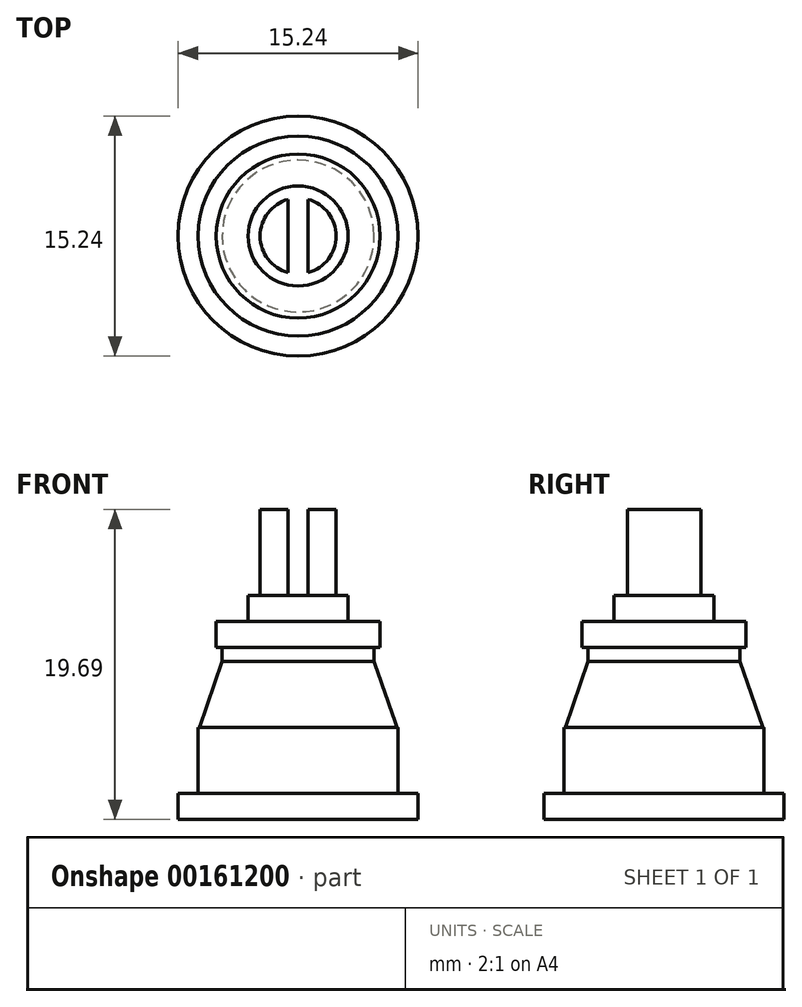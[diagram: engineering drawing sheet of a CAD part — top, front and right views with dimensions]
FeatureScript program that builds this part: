
annotation { "Feature Type Name" : "Feature", "Feature Type Description" : "" }
export const myFeature = defineFeature(function(context is Context, id is Id, definition is map)
    precondition{}
    {
        {
            var Q0;
            Q0=qCreatedBy(makeId("Front.planeOp"),FACE);
            var sketch = newSketch(context, id + "F0", { "sketchPlane" : qUnion([Q0])});
            skLineSegment(sketch, "E0", {"start": v(0, 29.57) * mm, "end": v(0, -1.96) * mm, "construction": true});
            skLineSegment(sketch, "E1", {"start": v(7.62, 0) * mm, "end": v(7.62, 1.65) * mm});
            skLineSegment(sketch, "E2", {"start": v(7.62, 1.65) * mm, "end": v(6.35, 1.65) * mm});
            skLineSegment(sketch, "E3", {"start": v(6.35, 1.65) * mm, "end": v(6.35, 5.84) * mm});
            skLineSegment(sketch, "E4", {"start": v(6.35, 5.84) * mm, "end": v(6.3, 5.84) * mm});
            skLineSegment(sketch, "E5", {"start": v(6.27, 5.86) * mm, "end": v(4.83, 10.03) * mm});
            skLineSegment(sketch, "E6", {"start": v(4.83, 10.03) * mm, "end": v(4.83, 10.03) * mm});
            skLineSegment(sketch, "E7", {"start": v(4.83, 10.03) * mm, "end": v(4.83, 10.92) * mm});
            skLineSegment(sketch, "E8", {"start": v(4.83, 10.92) * mm, "end": v(5.2, 10.92) * mm});
            skLineSegment(sketch, "E9", {"start": v(5.2, 10.92) * mm, "end": v(5.2, 12.57) * mm});
            skLineSegment(sketch, "E10", {"start": v(5.2, 12.57) * mm, "end": v(3.18, 12.57) * mm});
            skLineSegment(sketch, "E11", {"start": v(3.18, 12.57) * mm, "end": v(3.18, 14.22) * mm});
            skLineSegment(sketch, "E12", {"start": v(3.18, 14.22) * mm, "end": v(2.41, 14.22) * mm});
            skLineSegment(sketch, "E13", {"start": v(2.41, 14.22) * mm, "end": v(2.41, 19.69) * mm});
            skLineSegment(sketch, "E14", {"start": v(2.41, 19.69) * mm, "end": v(0, 19.69) * mm});
            skLineSegment(sketch, "E15", {"start": v(7.62, 0) * mm, "end": v(0, 0) * mm});
            skPoint(sketch, "E16.visualSharp", {"position": v(6.27, 5.84) * mm});
            skArc(sketch, "E16.filletArc", {"start": v(6.27, 5.86) * mm, "mid": v(6.28, 5.85) * mm, "end": v(6.3, 5.84) * mm});
            skLineSegment(sketch, "E17", {"start": v(0, 19.69) * mm, "end": v(0, 0) * mm});
            skLineSegment(sketch, "E18", {"start": v(0, 14.22) * mm, "end": v(0.64, 14.22) * mm});
            skLineSegment(sketch, "E19", {"start": v(0.64, 14.22) * mm, "end": v(0.64, 19.69) * mm});
            skLineSegment(sketch, "E20", {"start": v(0, 19.69) * mm, "end": v(-0.64, 19.69) * mm});
            skLineSegment(sketch, "E21", {"start": v(-0.64, 19.69) * mm, "end": v(-0.63, 14.22) * mm});
            skLineSegment(sketch, "E22", {"start": v(-0.63, 14.22) * mm, "end": v(0, 14.22) * mm});
            skSolve(sketch);
        }
        {
            var Q0;
            Q0=makeQuery(id+"F0.imprint","IMPRINT",FACE,{"disambiguationData":[TD([[makeQuery(id+"F0.imprint","IMPRINT",EDGE,{"derivedFrom":sQuery(id+"F0.wireOp",EDGE,"E1")}),1.0]])]});
            var Q1;
            Q1=sQuery(id+"F0.wireOp",EDGE,"E0");
            revolve(context, id + "F1", {"entities" : qUnion([Q0]), "axis" : qUnion([Q1]), "revolveType" : RevolveType.FULL});
        }
        {
            var Q0;
            {var subQ0=sQuery(id+"F0.wireOp",EDGE,"E20");Q0=makeQuery(id+"F0.imprint","IMPRINT",FACE,{"disambiguationData":[TD([[makeQuery(id+"F0.imprint","IMPRINT",EDGE,{"derivedFrom":subQ0}),1.0]])]});}
            var Q1;
            {var subQ4=sQuery(id+"F0.wireOp",EDGE,"E18");Q1=makeQuery(id+"F0.imprint","IMPRINT",FACE,{"disambiguationData":[TD([[makeQuery(id+"F0.imprint","IMPRINT",EDGE,{"derivedFrom":subQ4}),1.0]])]});}
            extrude(context, id + "F2", {"entities" : qUnion([Q0, Q1]), "operationType" : NewBodyOperationType.REMOVE, "endBound" : BoundingType.SYMMETRIC, "oppositeDirection" : true, "depth" : 6.35 * mm});
        }
    });
